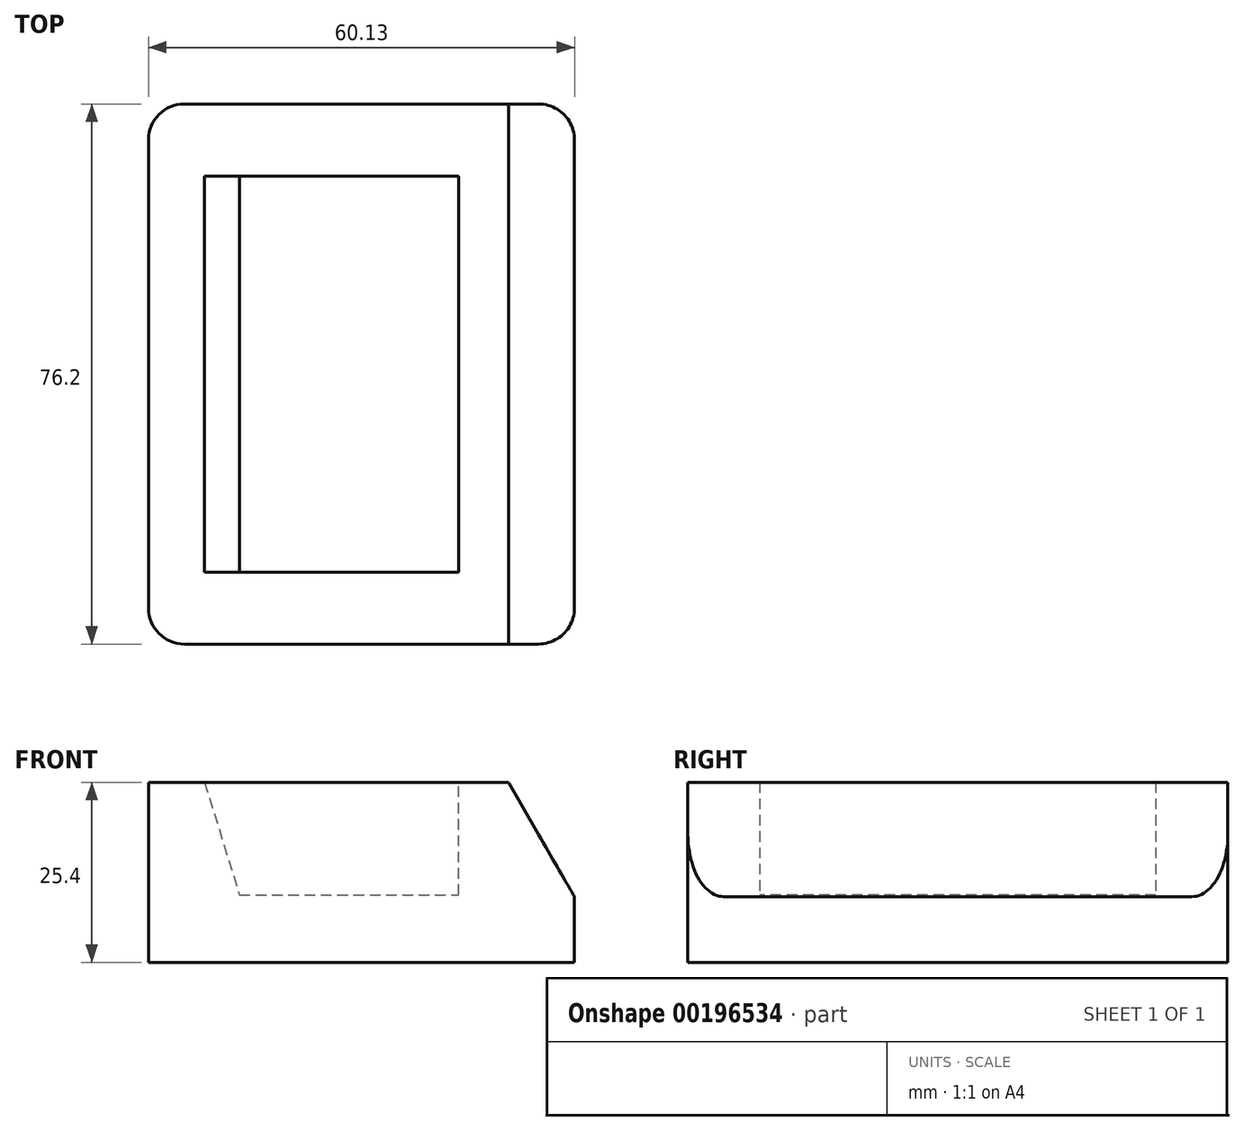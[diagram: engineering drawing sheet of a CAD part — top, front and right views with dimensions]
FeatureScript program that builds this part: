
annotation { "Feature Type Name" : "Feature", "Feature Type Description" : "" }
export const myFeature = defineFeature(function(context is Context, id is Id, definition is map)
    precondition{}
    {
        {
            var Q0;
            Q0=qCreatedBy(makeId("Front.planeOp"),FACE);
            var sketch = newSketch(context, id + "F0", { "sketchPlane" : qUnion([Q0])});
            skLineSegment(sketch, "E0", {"start": v(0, 0) * mm, "end": v(0, 25.4) * mm});
            skLineSegment(sketch, "E1", {"start": v(0, 25.4) * mm, "end": v(50.8, 25.4) * mm});
            skLineSegment(sketch, "E2", {"start": v(50.8, 25.4) * mm, "end": v(60.13, 9.25) * mm});
            skLineSegment(sketch, "E3", {"start": v(60.13, 0) * mm, "end": v(0, 0) * mm});
            skLineSegment(sketch, "E4", {"start": v(60.13, 9.25) * mm, "end": v(60.13, 0) * mm});
            skPoint(sketch, "E5.orphan", {"position": v(65.46, 0) * mm});
            skSolve(sketch);
        }
        {
            var Q0;
            Q0=makeQuery(id+"F0.imprint","IMPRINT",FACE,{"disambiguationData":[TD([[makeQuery(id+"F0.imprint","IMPRINT",EDGE,{"derivedFrom":sQuery(id+"F0.wireOp",EDGE,"E0")}),-1.0]])]});
            extrude(context, id + "F1", {"entities" : qUnion([Q0]), "endBound" : BoundingType.SYMMETRIC, "depth" : 76.2 * mm});
        }
        {
            var Q0;
            Q0=qCreatedBy(makeId("Front.planeOp"),FACE);
            var sketch = newSketch(context, id + "F2", { "sketchPlane" : qUnion([Q0])});
            skLineSegment(sketch, "E6", {"start": v(7.93, 25.4) * mm, "end": v(12.84, 9.51) * mm});
            skLineSegment(sketch, "E7", {"start": v(12.84, 9.51) * mm, "end": v(43.76, 9.51) * mm});
            skLineSegment(sketch, "E8", {"start": v(43.76, 9.51) * mm, "end": v(43.76, 25.4) * mm});
            skLineSegment(sketch, "E9", {"start": v(43.76, 25.4) * mm, "end": v(7.93, 25.4) * mm});
            skSolve(sketch);
        }
        {
            var Q0;
            Q0 = qSketchRegion(id + "F2", true);
            extrude(context, id + "F3", {"entities" : qUnion([Q0]), "operationType" : NewBodyOperationType.REMOVE, "endBound" : BoundingType.SYMMETRIC, "oppositeDirection" : true, "depth" : 55.88 * mm});
        }
        {
            var Q0;
            Q0=makeQuery(id+"F1.opExtrude","CAP_EDGE",EDGE,{"disambiguationData":[OSD([sQuery(id+"F0.wireOp",EDGE,"E0")])],"isStart":false});
            var Q1;
            Q1=makeQuery(id+"F1.opExtrude","CAP_EDGE",EDGE,{"disambiguationData":[OSD([sQuery(id+"F0.wireOp",EDGE,"E4")])],"isStart":false});
            var Q2;
            Q2=makeQuery(id+"F1.opExtrude","CAP_EDGE",EDGE,{"disambiguationData":[OSD([sQuery(id+"F0.wireOp",EDGE,"E4")])],"isStart":true});
            var Q3;
            Q3=makeQuery(id+"F1.opExtrude","CAP_EDGE",EDGE,{"disambiguationData":[OSD([sQuery(id+"F0.wireOp",EDGE,"E0")])],"isStart":true});
            fillet(context, id + "F4", {"entities" : qUnion([Q0, Q1, Q2, Q3]), "radius" : 5.08 * mm, "tangentPropagation" : true, "allowEdgeOverflow" : false});
        }
    });
